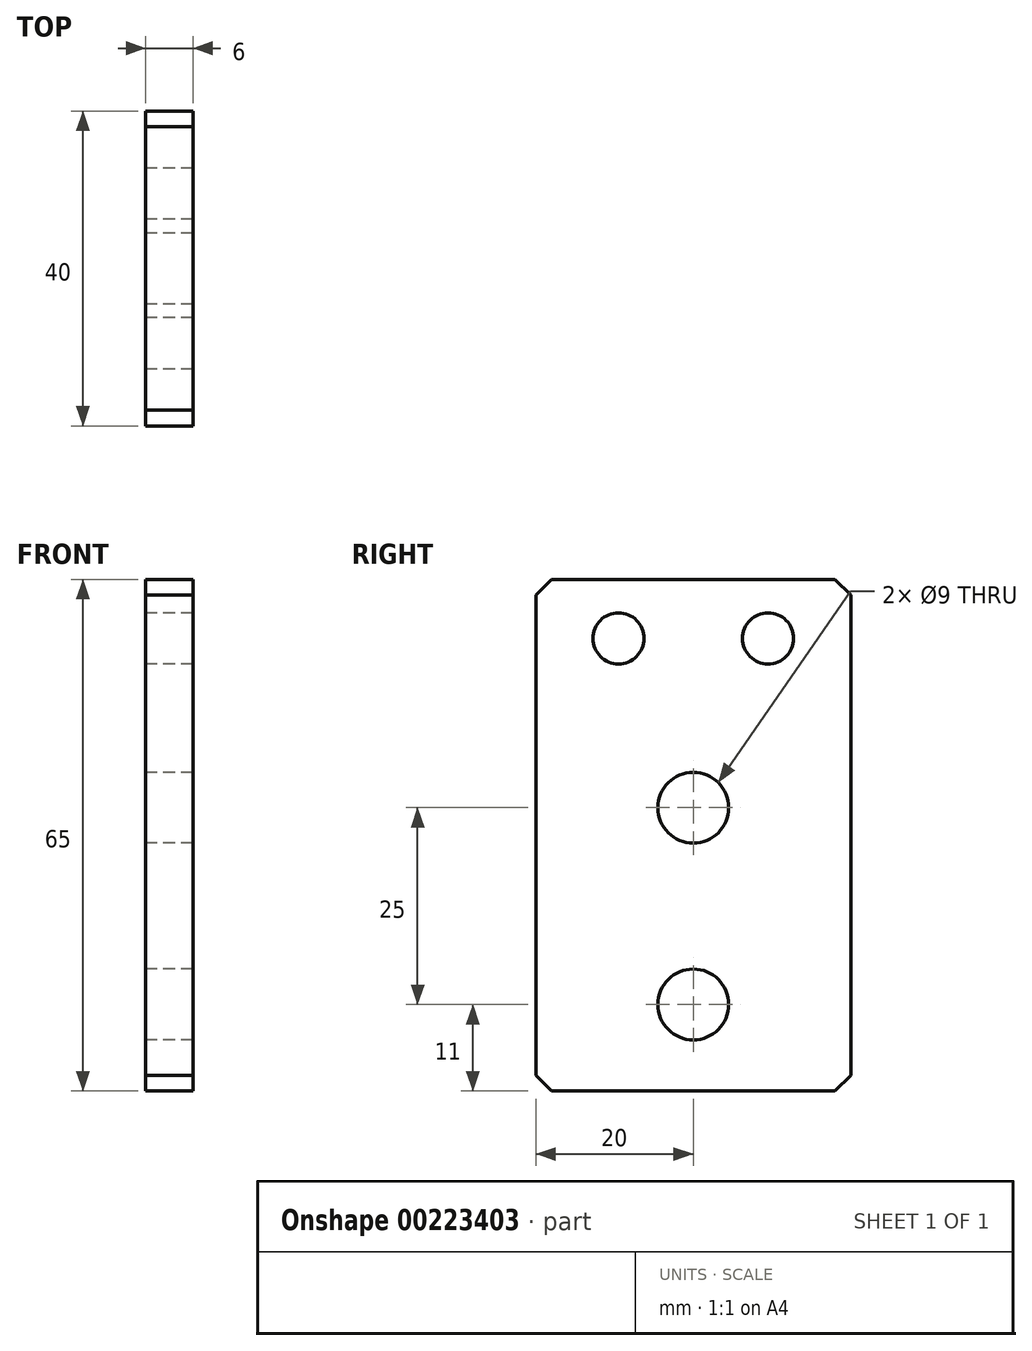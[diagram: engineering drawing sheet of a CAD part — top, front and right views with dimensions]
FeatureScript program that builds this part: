
annotation { "Feature Type Name" : "Feature", "Feature Type Description" : "" }
export const myFeature = defineFeature(function(context is Context, id is Id, definition is map)
    precondition{}
    {
        {
            var Q0;
            Q0=qCreatedBy(makeId("Right.planeOp"),FACE);
            var sketch = newSketch(context, id + "F0", { "sketchPlane" : qUnion([Q0])});
            skLineSegment(sketch, "E0.bottom", {"start": v(0, 0) * mm, "end": v(40, 0) * mm});
            skLineSegment(sketch, "E0.top", {"start": v(0, -65) * mm, "end": v(40, -65) * mm});
            skLineSegment(sketch, "E0.left", {"start": v(0, 0) * mm, "end": v(0, -65) * mm});
            skLineSegment(sketch, "E0.right", {"start": v(40, 0) * mm, "end": v(40, -65) * mm});
            skCircle(sketch, "E1", {"center": v(20, -29) * mm, "radius": 4.5 * mm});
            skCircle(sketch, "E2", {"center": v(20, -54) * mm, "radius": 4.5 * mm});
            skCircle(sketch, "E3", {"center": v(10.5, -7.5) * mm, "radius": 3.25 * mm});
            skCircle(sketch, "E4", {"center": v(29.5, -7.5) * mm, "radius": 3.25 * mm});
            skSolve(sketch);
        }
        {
            var Q0;
            Q0 = qSketchRegion(id + "F0", true);
            extrude(context, id + "F1", {"entities" : qUnion([Q0]), "depth" : 6 * mm});
        }
        {
            var Q0;
            Q0=makeQuery(id+"F1.opExtrude","SWEPT_EDGE",EDGE,{"disambiguationData":[OSD([sQuery(id+"F0.wireOp",EDGE,"E0.top"),sQuery(id+"F0.wireOp",EDGE,"E0.left")])]});
            var Q1;
            Q1=makeQuery(id+"F1.opExtrude","SWEPT_EDGE",EDGE,{"disambiguationData":[OSD([sQuery(id+"F0.wireOp",EDGE,"E0.top"),sQuery(id+"F0.wireOp",EDGE,"E0.right")])]});
            var Q2;
            Q2=makeQuery(id+"F1.opExtrude","SWEPT_EDGE",EDGE,{"disambiguationData":[OSD([sQuery(id+"F0.wireOp",EDGE,"E0.bottom"),sQuery(id+"F0.wireOp",EDGE,"E0.right")])]});
            var Q3;
            Q3=makeQuery(id+"F1.opExtrude","SWEPT_EDGE",EDGE,{"disambiguationData":[OSD([sQuery(id+"F0.wireOp",EDGE,"E0.bottom"),sQuery(id+"F0.wireOp",EDGE,"E0.left")])]});
            chamfer(context, id + "F2", {"entities" : qUnion([Q0, Q1, Q2, Q3]), "width" : 2 * mm, "tangentPropagation" : true});
        }
    });
